# Revit family: HL_Механический канализационный затвор_HL712.1
name_source: partatom
category: Příslušenství trubek
revit_build: Autodesk Revit 2016 (Build: 20151007_0715(x64)
units: mm (PartAtom-declared; Revit-internal decimal feet)

## family parameters
Kóta kulaté spojky = Použít průměr
Nadpis OmniClass = Non-Return Valves for Liquid Services
Ořezat dutým tvarem při načtení = Ne
Sdílené = Ne
Typ součásti = Normální
Vždy vertikální = Ano
Založené na pracovní rovině = Ne
Číslo OmniClass = 23.65.55.14.21

## types (1)
- HL_Механический канализационный затвор_HL712.1
    Cena = 0 $
    EAN = 9003076971213
    Klíčová poznámka = HL712.1
    Komentáře k typům = Механический канализационный затвор DN125 с заслонкой из нержавеющей стали и ручным затвором
    Model = HL712.1
    Popis = Механический канализационный затвор
    URL = http://www.hutterer-lechner.com
    Výrobce = HL Hutterer & Lechner GmbH
    ВЕС = 2,235 kg
    ВЫСОТА МОНТАЖА = 320 mm
    МАТЕРИАЛ = ABS
    НОМИНАЛЬНЫЙ ДИАМЕТР = 125 mm
    НОМИНАЛЬНЫЙ ДИАМЕТР 2 = 125 mm
    РАЗМЕР = DN125
